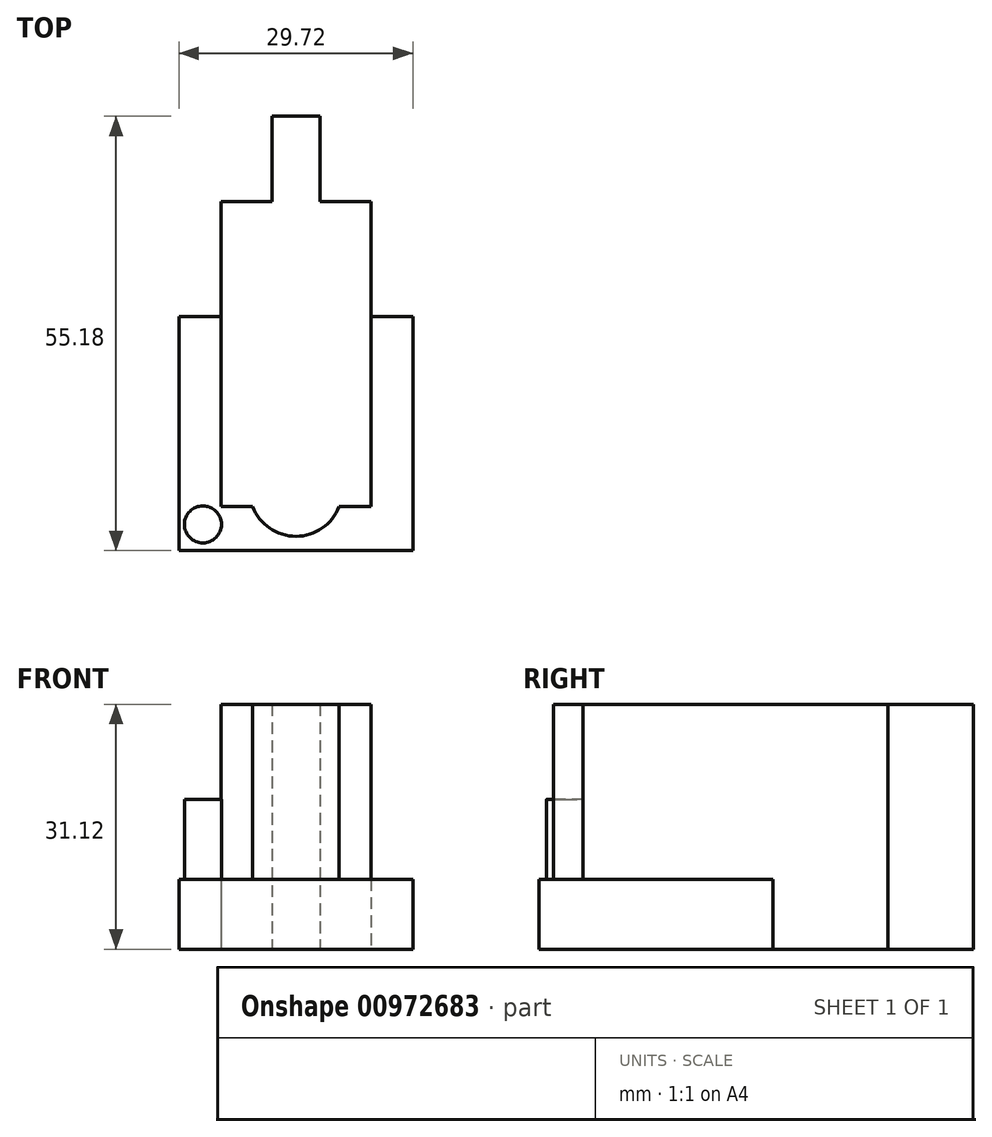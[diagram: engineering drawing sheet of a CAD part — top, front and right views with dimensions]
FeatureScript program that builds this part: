
annotation { "Feature Type Name" : "Feature", "Feature Type Description" : "" }
export const myFeature = defineFeature(function(context is Context, id is Id, definition is map)
    precondition{}
    {
        {
            var Q0;
            Q0=qCreatedBy(makeId("Top.planeOp"),FACE);
            var sketch = newSketch(context, id + "F0", { "sketchPlane" : qUnion([Q0])});
            skLineSegment(sketch, "E0.top", {"start": v(-37.6, -11.55) * mm, "end": v(-7.9, -11.55) * mm});
            skLineSegment(sketch, "E0.left", {"start": v(-37.6, 18.17) * mm, "end": v(-37.6, -11.55) * mm});
            skLineSegment(sketch, "E0.right", {"start": v(-7.9, 18.17) * mm, "end": v(-7.9, -11.55) * mm});
            skLineSegment(sketch, "E1.bottom", {"start": v(-25.8, 43.63) * mm, "end": v(-19.69, 43.63) * mm});
            skLineSegment(sketch, "E1.left", {"start": v(-25.8, 43.63) * mm, "end": v(-25.8, 32.8) * mm});
            skLineSegment(sketch, "E1.right", {"start": v(-19.69, 43.63) * mm, "end": v(-19.69, 32.8) * mm});
            skLineSegment(sketch, "E2.left", {"start": v(-32.27, 32.8) * mm, "end": v(-32.27, -5.94) * mm});
            skLineSegment(sketch, "E2.right", {"start": v(-13.22, 32.8) * mm, "end": v(-13.22, -5.94) * mm});
            skLineSegment(sketch, "E3", {"start": v(-37.6, 18.17) * mm, "end": v(-32.27, 18.17) * mm});
            skLineSegment(sketch, "E4", {"start": v(-7.9, 18.17) * mm, "end": v(-13.22, 18.17) * mm});
            skCircle(sketch, "E5", {"center": v(-34.56, -8.21) * mm, "radius": 2.35 * mm});
            skArc(sketch, "E6", {"start": v(-28.25, -5.94) * mm, "mid": v(-22.75, -9.72) * mm, "end": v(-17.25, -5.94) * mm});
            skLineSegment(sketch, "E7", {"start": v(-32.27, -5.94) * mm, "end": v(-28.25, -5.94) * mm});
            skLineSegment(sketch, "E8", {"start": v(-17.25, -5.94) * mm, "end": v(-13.22, -5.94) * mm});
            skLineSegment(sketch, "E9", {"start": v(-25.8, 32.8) * mm, "end": v(-32.27, 32.8) * mm});
            skLineSegment(sketch, "E10", {"start": v(-13.22, 32.8) * mm, "end": v(-19.69, 32.8) * mm});
            skSolve(sketch);
        }
        {
            var Q0;
            Q0=makeQuery(id+"F0.imprint","IMPRINT",FACE,{"disambiguationData":[TD([[makeQuery(id+"F0.imprint","IMPRINT",EDGE,{"derivedFrom":sQuery(id+"F0.wireOp",EDGE,"E1.bottom")}),-1.0]])]});
            extrude(context, id + "F1", {"entities" : qUnion([Q0]), "depth" : 31.12 * mm, "offsetDistance" : 25.4 * mm});
        }
        {
            var Q0;
            Q0=makeQuery(id+"F0.imprint","IMPRINT",FACE,{"disambiguationData":[TD([[makeQuery(id+"F0.imprint","IMPRINT",EDGE,{"derivedFrom":sQuery(id+"F0.wireOp",EDGE,"E0.top")}),1.0]])]});
            extrude(context, id + "F2", {"entities" : qUnion([Q0]), "operationType" : NewBodyOperationType.ADD, "depth" : 8.9 * mm, "offsetDistance" : 25.4 * mm});
        }
        {
            var Q0;
            Q0=makeQuery(id+"F0.imprint","IMPRINT",FACE,{"disambiguationData":[TD([[makeQuery(id+"F0.imprint","IMPRINT",EDGE,{"derivedFrom":sQuery(id+"F0.wireOp",EDGE,"E5")}),1.0]])]});
            extrude(context, id + "F3", {"entities" : qUnion([Q0]), "operationType" : NewBodyOperationType.ADD, "depth" : 19.05 * mm, "offsetDistance" : 25.4 * mm});
        }
    });
